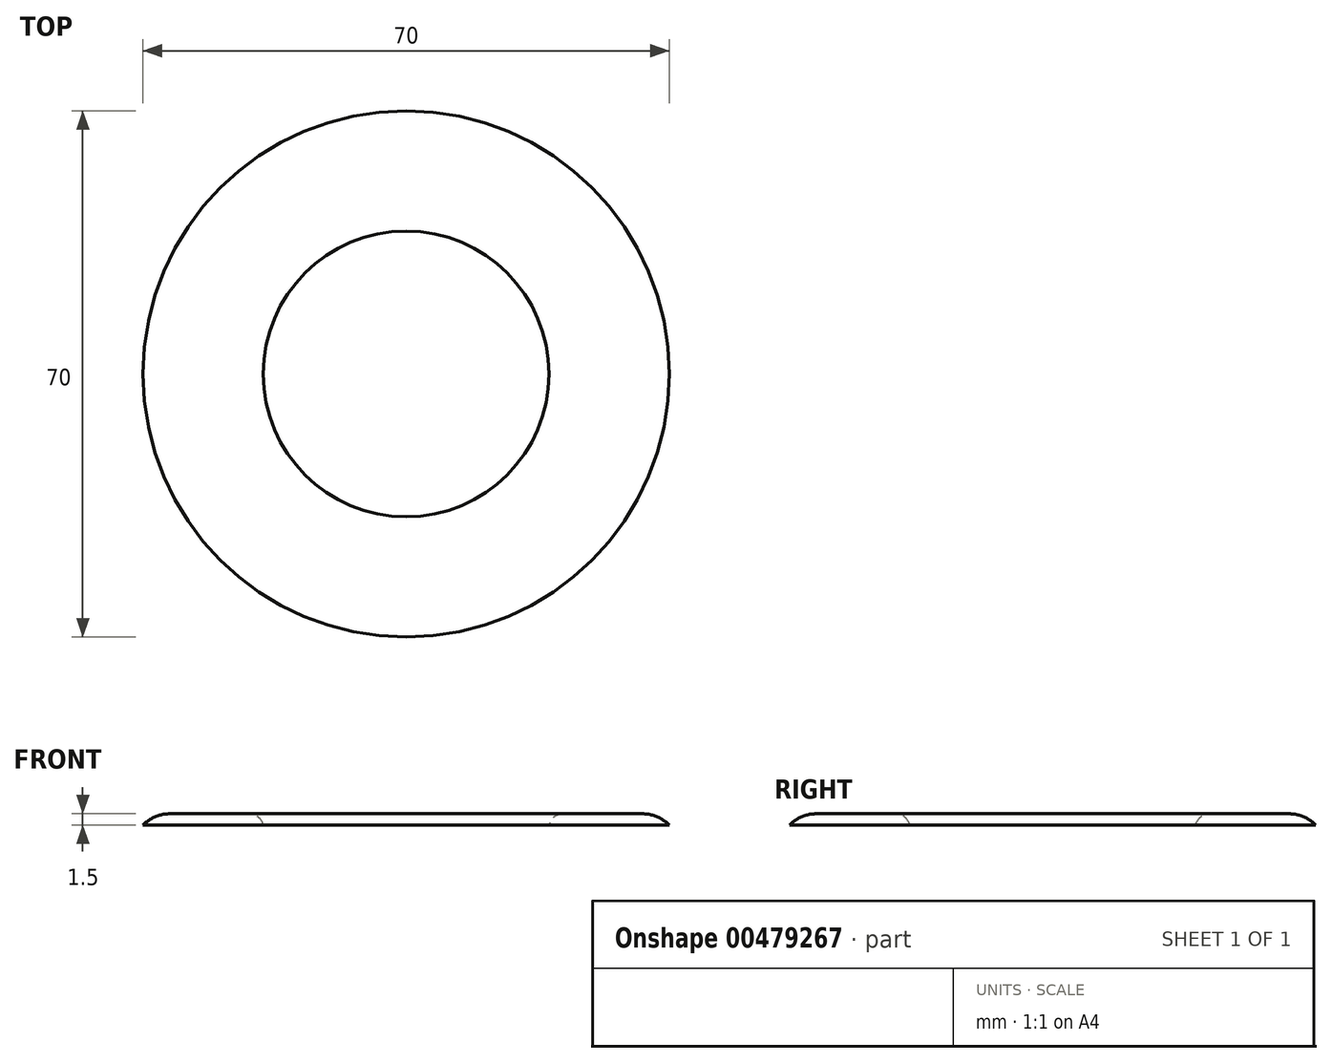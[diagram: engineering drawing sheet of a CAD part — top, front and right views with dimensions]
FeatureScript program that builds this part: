
annotation { "Feature Type Name" : "Feature", "Feature Type Description" : "" }
export const myFeature = defineFeature(function(context is Context, id is Id, definition is map)
    precondition{}
    {
        {
            var Q0;
            Q0=qCreatedBy(makeId("Top.planeOp"),FACE);
            var sketch = newSketch(context, id + "F0", { "sketchPlane" : qUnion([Q0])});
            skCircle(sketch, "E0", {"center": v(0, 0) * mm, "radius": 35 * mm});
            skCircle(sketch, "E1", {"center": v(0, 0) * mm, "radius": 19 * mm});
            skSolve(sketch);
        }
        {
            var Q0;
            Q0 = qSketchRegion(id + "F0", true);
            extrude(context, id + "F1", {"entities" : qUnion([Q0]), "depth" : 1.5 * mm});
        }
        {
            var Q0;
            Q0=makeQuery(id+"F1.opExtrude","CAP_EDGE",EDGE,{"disambiguationData":[OSD([sQuery(id+"F0.wireOp",EDGE,"E1")])],"isStart":false});
            fillet(context, id + "F2", {"entities" : qUnion([Q0]), "radius" : 2 * mm, "tangentPropagation" : true, "allowEdgeOverflow" : false});
        }
        {
            var Q0;
            Q0=makeQuery(id+"F1.opExtrude","CAP_EDGE",EDGE,{"disambiguationData":[OSD([sQuery(id+"F0.wireOp",EDGE,"E0")])],"isStart":false});
            fillet(context, id + "F3", {"entities" : qUnion([Q0]), "radius" : 5 * mm, "tangentPropagation" : true, "allowEdgeOverflow" : false});
        }
    });
